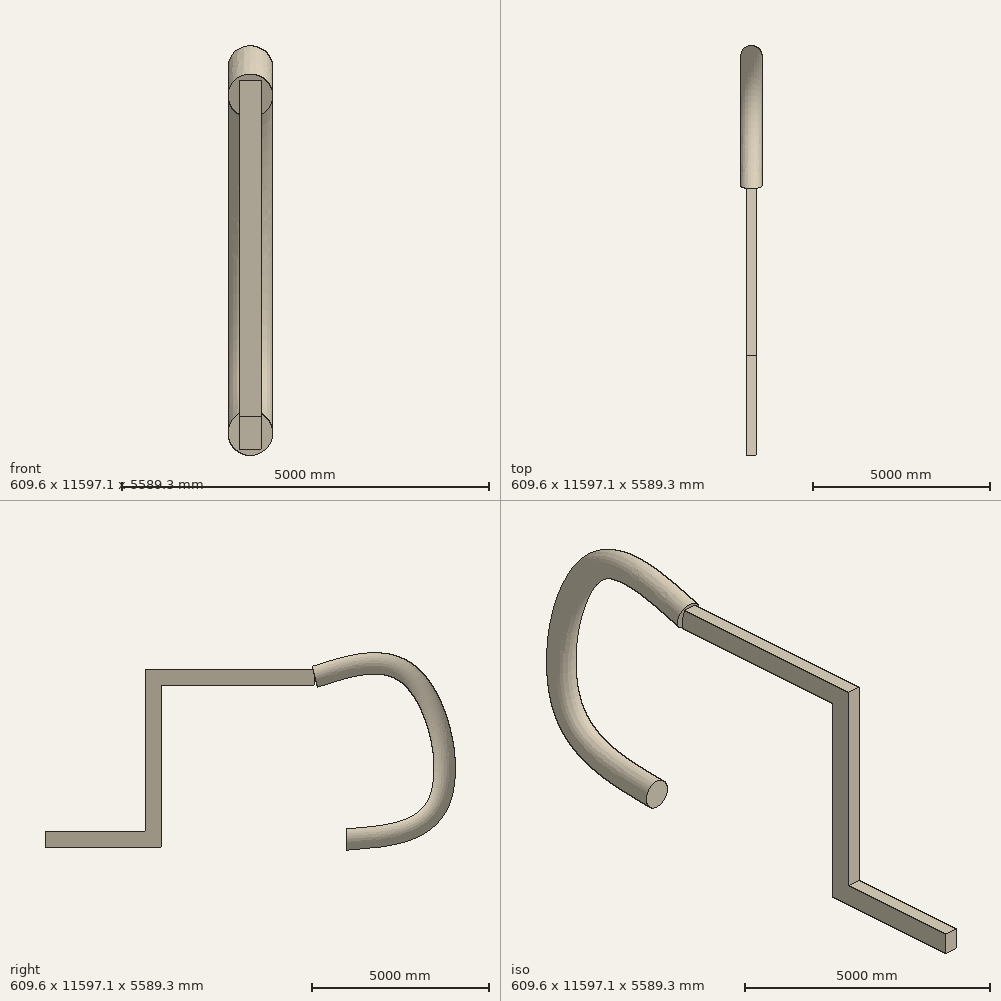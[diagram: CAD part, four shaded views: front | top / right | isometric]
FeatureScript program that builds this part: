
annotation { "Feature Type Name" : "Feature", "Feature Type Description" : "" }
export const myFeature = defineFeature(function(context is Context, id is Id, definition is map)
    precondition{}
    {
        {
            var Q0;
            Q0=qCreatedBy(makeId("Right.planeOp"),FACE);
            var sketch = newSketch(context, id + "F0", { "sketchPlane" : qUnion([Q0])});
            skLineSegment(sketch, "E0", {"start": v(-7885.81, 0) * mm, "end": v(-4837.81, 0) * mm});
            skLineSegment(sketch, "E1", {"start": v(-4837.81, 0) * mm, "end": v(-4837.81, 4572) * mm});
            skLineSegment(sketch, "E2", {"start": v(-4837.81, 4572) * mm, "end": v(-265.81, 4572) * mm});
            skSolve(sketch);
        }
        {
            var Q0;
            Q0=qCreatedBy(makeId("Front.planeOp"),FACE);
            var Q1;
            Q1=sQuery(id+"F0.wireOp",VERTEX,"E0.start");
            cPlane(context, id + "F1", {"entities" : qUnion([Q0, Q1]), "cplaneType" : CPlaneType.PLANE_POINT, "offset" : 25.4 * mm, "width" : 152.4 * mm, "height" : 152.4 * mm});
        }
        {
            var Q0;
            Q0=qCreatedBy(id+"F1.planeOp",FACE);
            var sketch = newSketch(context, id + "F2", { "sketchPlane" : qUnion([Q0])});
            skLineSegment(sketch, "E3.bottom", {"start": v(152.4, -228.6) * mm, "end": v(-152.4, -228.6) * mm});
            skLineSegment(sketch, "E3.top", {"start": v(152.4, 228.6) * mm, "end": v(-152.4, 228.6) * mm});
            skLineSegment(sketch, "E3.left", {"start": v(152.4, -228.6) * mm, "end": v(152.4, 228.6) * mm});
            skLineSegment(sketch, "E3.right", {"start": v(-152.4, -228.6) * mm, "end": v(-152.4, 228.6) * mm});
            skPoint(sketch, "E3.middle", {"position": v(0, 0) * mm});
            skSolve(sketch);
        }
        {
            var Q0;
            Q0=makeQuery(id+"F2.imprint","IMPRINT",FACE,{"disambiguationData":[TD([[makeQuery(id+"F2.imprint","IMPRINT",EDGE,{"derivedFrom":sQuery(id+"F2.wireOp",EDGE,"E3.bottom")}),-1.0]])]});
            var Q1;
            Q1=sQuery(id+"F0.wireOp",EDGE,"E0");
            var Q2;
            Q2=sQuery(id+"F0.wireOp",EDGE,"E1");
            var Q3;
            Q3=sQuery(id+"F0.wireOp",EDGE,"E2");
            sweep(context, id + "F3", {"profiles" : qUnion([Q0]), "path" : qUnion([Q1, Q2, Q3])});
        }
        {
            var Q0;
            Q0=qCreatedBy(makeId("Right.planeOp"),FACE);
            var sketch = newSketch(context, id + "F4", { "sketchPlane" : qUnion([Q0])});
            skFitSpline(sketch, "E4", {"points": [v(-265.81, 4596.6) * mm, v(2411.47, 4647.05) * mm, v(3211.05, 984.9) * mm, v(636.05, 0) * mm], "startDerivative": vector(9422.42, 3115.4) * mm, "endDerivative": vector(-10235.18, -730.64) * mm});
            skSolve(sketch);
        }
        {
            var Q0;
            Q0=sQuery(id+"F4.wireOp",VERTEX,"E4.end");
            var Q1;
            Q1=qCreatedBy(makeId("Front.planeOp"),FACE);
            cPlane(context, id + "F5", {"entities" : qUnion([Q0, Q1]), "cplaneType" : CPlaneType.PLANE_POINT, "offset" : 25.4 * mm, "width" : 152.4 * mm, "height" : 152.4 * mm});
        }
        {
            var Q0;
            Q0=qCreatedBy(id+"F5.planeOp",FACE);
            var sketch = newSketch(context, id + "F6", { "sketchPlane" : qUnion([Q0])});
            skCircle(sketch, "E5", {"center": v(0, 0) * mm, "radius": 304.8 * mm});
            skSolve(sketch);
        }
        {
            var Q0;
            Q0=makeQuery(id+"F6.imprint","IMPRINT",FACE,{"disambiguationData":[TD([[makeQuery(id+"F6.imprint","IMPRINT",EDGE,{"derivedFrom":sQuery(id+"F6.wireOp",EDGE,"E5")}),1.0]])]});
            var Q1;
            Q1=sQuery(id+"F4.wireOp",EDGE,"E4");
            sweep(context, id + "F7", {"operationType" : NewBodyOperationType.ADD, "profiles" : qUnion([Q0]), "path" : qUnion([Q1])});
        }
    });
